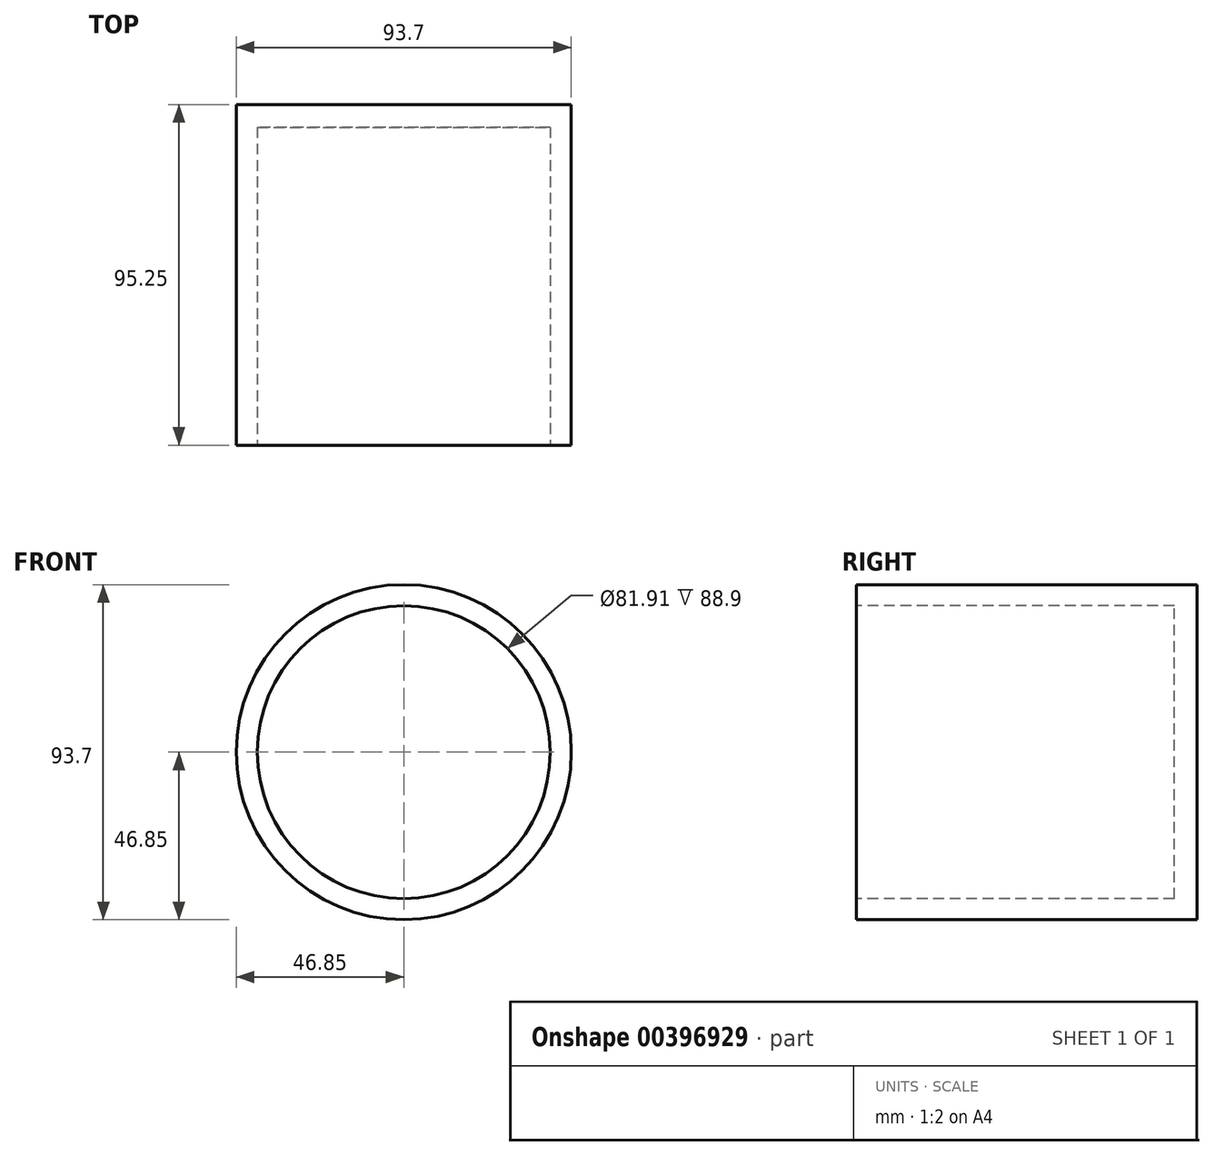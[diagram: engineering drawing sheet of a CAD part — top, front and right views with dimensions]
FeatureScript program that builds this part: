
annotation { "Feature Type Name" : "Feature", "Feature Type Description" : "" }
export const myFeature = defineFeature(function(context is Context, id is Id, definition is map)
    precondition{}
    {
        {
            var Q0;
            Q0=qCreatedBy(makeId("Front.planeOp"),FACE);
            var sketch = newSketch(context, id + "F0", { "sketchPlane" : qUnion([Q0])});
            skCircle(sketch, "E0", {"center": v(0, 0) * mm, "radius": 46.85 * mm});
            skSolve(sketch);
        }
        {
            var Q0;
            Q0=makeQuery(id+"F0.imprint","IMPRINT",FACE,{"disambiguationData":[TD([[makeQuery(id+"F0.imprint","IMPRINT",EDGE,{"derivedFrom":sQuery(id+"F0.wireOp",EDGE,"E0")}),1.0]])]});
            var Q1;
            Q1 = qSketchRegion(id + "F0", true);
            extrude(context, id + "F1", {"entities" : qUnion([Q0, Q1]), "depth" : 95.25 * mm});
        }
        {
            var Q0;
            Q0=makeQuery(id+"F1.opExtrude","CAP_FACE",FACE,{"disambiguationData":[OSD([sQuery(id+"F0.wireOp",EDGE,"E0")])],"isStart":false});
            var sketch = newSketch(context, id + "F2", { "sketchPlane" : qUnion([Q0])});
            skCircle(sketch, "E1", {"center": v(0, 0) * mm, "radius": 40.96 * mm});
            skSolve(sketch);
        }
        {
            var Q0;
            Q0=makeQuery(id+"F2.imprint","IMPRINT",FACE,{"disambiguationData":[TD([[makeQuery(id+"F2.imprint","IMPRINT",EDGE,{"derivedFrom":sQuery(id+"F2.wireOp",EDGE,"E1")}),1.0]])]});
            extrude(context, id + "F3", {"entities" : qUnion([Q0]), "operationType" : NewBodyOperationType.REMOVE, "oppositeDirection" : true, "depth" : 88.9 * mm});
        }
    });
